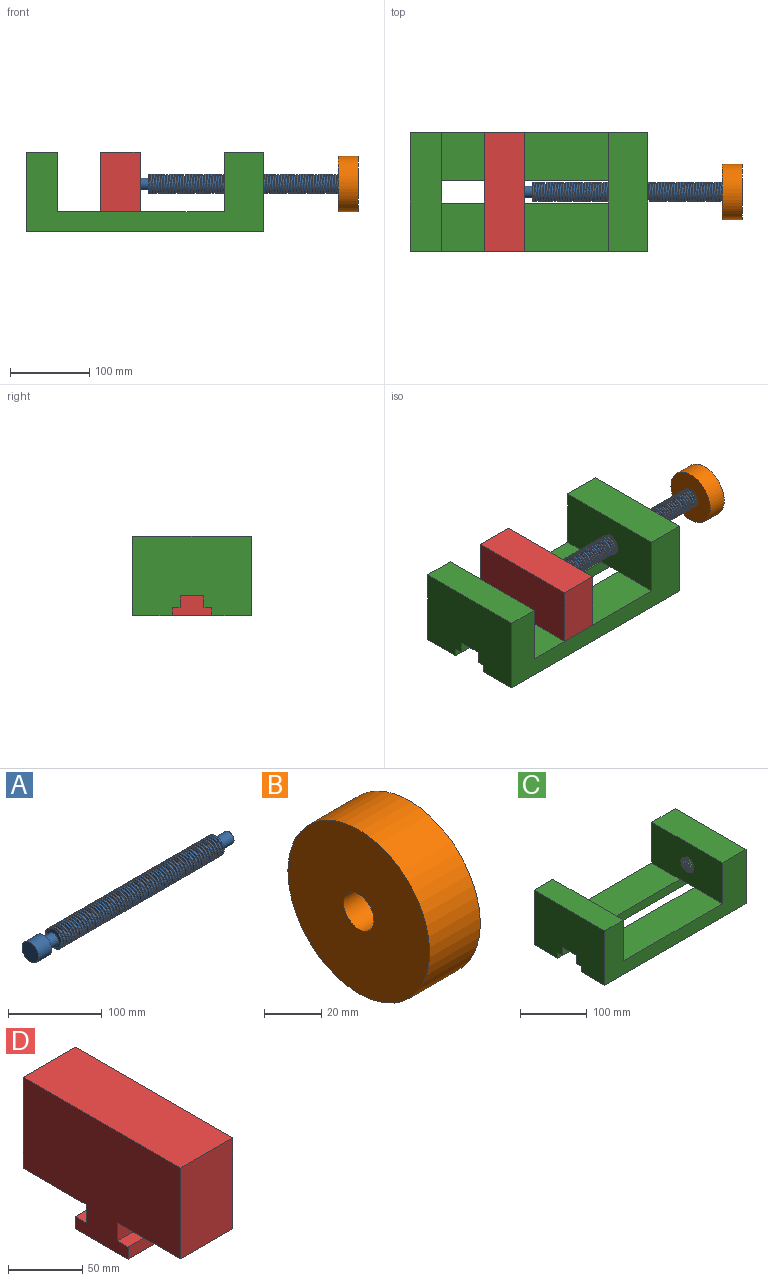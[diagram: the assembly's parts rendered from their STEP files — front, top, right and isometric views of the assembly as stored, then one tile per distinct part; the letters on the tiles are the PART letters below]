
ASSEMBLY  parts=4 mates=3
PART A: 12 faces, bbox 300x28.9x25 mm
  f0: cylinder r=12.5mm len=245mm, axis (-1,0,0), area 9606.8mm2, adj f5,f6,f10,f11
  f1: cylinder r=12.5mm len=25mm, axis (-1,0,0), area 1570.8mm2, adj f2,f3
  f2: plane 25x25mm, normal (-1,0,0), area 490.9mm2, adj f1
  f3: plane 25x25mm, normal (1,0,0), area 314.2mm2, adj f1,f4
  f4: cylinder r=7.5mm len=15mm, axis (-1,0,0), area 706.9mm2, adj f3,f5
  f5: plane 25x23mm, normal (-1,0,0), area 241.9mm2, adj f0,f4,f9,f10,f11
  f6: plane 25x23mm, normal (1,0,0), area 241.9mm2, adj f0,f7,f9,f10,f11
  f7: cylinder r=7.5mm len=20mm, axis (-1,0,0), area 942.5mm2, adj f6,f8
  f8: plane 15x15mm, normal (1,0,0), area 176.7mm2, adj f7
  f9: cylinder r=10.5mm len=245mm, axis (-1,0,0), area 8069.7mm2, adj f5,f6,f10,f11
  f10: bspline ~245.33x28.87mm, area 8865.3mm2, adj f0,f5,f6,f9
  f11: bspline ~246x28.87mm, area 8865.3mm2, adj f0,f5,f6,f9
PART B: 4 faces, bbox 25x70x70 mm
  f0: cylinder r=7.5mm len=25mm, axis (1,0,0), area 1178.1mm2, adj f2,f3
  f1: cylinder r=35mm len=70mm, axis (1,0,0), area 5497.8mm2, adj f2,f3
  f2: plane 70x70mm, normal (-1,0,0), area 3671.7mm2, adj f0,f1
  f3: plane 70x70mm, normal (1,0,0), area 3671.7mm2, adj f0,f1
PART C: 24 faces, bbox 300.7x150x100 mm
  f0: cylinder r=12mm len=50mm, axis (1,0,0), area 1890.9mm2, adj f6,f12,f22,f23
  f1: plane 300x50mm, normal (0,0,-1), area 15000mm2, adj f3,f6,f7,f14
  f2: plane 210x60mm, normal (0,0,1), area 12600mm2, adj f7,f10,f12,f16
  f3: plane 150x100mm, normal (-1,0,0), area 14050mm2, adj f1,f5,f7,f8,f9,f13,f14,f15
  f4: plane 150x50mm, normal (0,0,1), area 7500mm2, adj f5,f6,f7,f12
  f5: plane 300x100mm, normal (0,-1,0), area 14250mm2, adj f3,f4,f6,f8,f9,f10,f11,f12
  f6: plane 150x100mm, normal (1,0,0), area 13515.9mm2, adj f0,f1,f4,f5,f7,f9,f14,f15
  f7: plane 300x100mm, normal (0,1,0), area 14250mm2, adj f1,f2,f3,f4,f6,f8,f10,f12
  f8: plane 150x40mm, normal (0,0,1), area 6000mm2, adj f3,f5,f7,f10
  f9: plane 300x50mm, normal (0,0,-1), area 15000mm2, adj f3,f5,f6,f20
  f10: plane 150x75mm, normal (1,0,0), area 11250mm2, adj f2,f5,f7,f8,f11,f13
  f11: plane 210x60mm, normal (0,0,1), area 12600mm2, adj f5,f10,f12,f18
  f12: plane 150x75mm, normal (-1,0,0), area 10715.9mm2, adj f0,f2,f4,f5,f7,f11,f17,f21
  f13: plane 40x30mm, normal (0,0,-1), area 1200mm2, adj f3,f10,f16,f18
  f14: plane 300x10mm, normal (0,-1,0), area 3000mm2, adj f1,f3,f6,f15
  f15: plane 300x10mm, normal (0,0,-1), area 3000mm2, adj f3,f6,f14,f16
  f16: plane 300x15mm, normal (0,-1,0), area 4500mm2, adj f2,f3,f6,f13,f15,f17
  f17: plane 50x30mm, normal (0,0,-1), area 1500mm2, adj f6,f12,f16,f18
  f18: plane 300x15mm, normal (0,1,0), area 4500mm2, adj f3,f6,f11,f13,f17,f19
  f19: plane 300x10mm, normal (0,0,-1), area 3000mm2, adj f3,f6,f18,f20
  f20: plane 300x10mm, normal (0,1,0), area 3000mm2, adj f3,f6,f9,f19
  f21: cylinder r=14mm len=50mm, axis (-1,0,0), area 2206mm2, adj f6,f12,f22,f23
  f22: bspline ~50.67x32.33mm, area 2049.1mm2, adj f0,f6,f12,f21
  f23: bspline ~50x32.33mm, area 2049.1mm2, adj f0,f6,f12,f21
PART D: 16 faces, bbox 50x150x100 mm
  f0: plane 75x50mm, normal (0,1,0), area 3750mm2, adj f1,f11,f12,f13
  f1: plane 150x50mm, normal (0,0,1), area 7500mm2, adj f0,f2,f12,f13
  f2: plane 75x50mm, normal (0,-1,0), area 3750mm2, adj f1,f3,f12,f13
  f3: plane 60x50mm, normal (0,0,-1), area 3000mm2, adj f2,f4,f12,f13
  f4: plane 50x15mm, normal (0,-1,0), area 750mm2, adj f3,f5,f12,f13
  f5: plane 50x10mm, normal (0,0,1), area 500mm2, adj f4,f6,f12,f13
  f6: plane 50x10mm, normal (0,-1,0), area 500mm2, adj f5,f7,f12,f13
  f7: plane 50x50mm, normal (0,0,-1), area 2500mm2, adj f6,f8,f12,f13
  f8: plane 50x10mm, normal (0,1,0), area 500mm2, adj f7,f9,f12,f13
  f9: plane 50x10mm, normal (0,0,1), area 500mm2, adj f8,f10,f12,f13
  f10: plane 50x15mm, normal (0,1,0), area 750mm2, adj f9,f11,f12,f13
  f11: plane 60x50mm, normal (0,0,-1), area 3000mm2, adj f0,f10,f12,f13
  f12: plane 150x100mm, normal (1,0,0), area 11709.1mm2, adj f0,f1,f2,f3,f4,f5,f6,f7
  f13: plane 150x100mm, normal (-1,0,0), area 12200mm2, adj f0,f1,f2,f3,f4,f5,f6,f7
  f14: cylinder r=12.5mm len=25mm, axis (1,0,0), area 1963.5mm2, adj f12,f15
  f15: plane 25x25mm, normal (1,0,0), area 490.9mm2, adj f14
PLACE A t=(204,75,0)mm
PLACE B t=(204,75,0)mm
PLACE C t=(150,75,0)mm
PLACE D t=(204,75,0)mm
MATE slider C.f10 <-> D.f13  axis (1,0,0) through (40,0,25)mm
MATE revolute B.f0 <-> A.f4  axis (1,0,0) through (419,75,60)mm
MATE revolute D.f14 <-> A.f4  axis (1,0,0) through (119,75,60)mm
